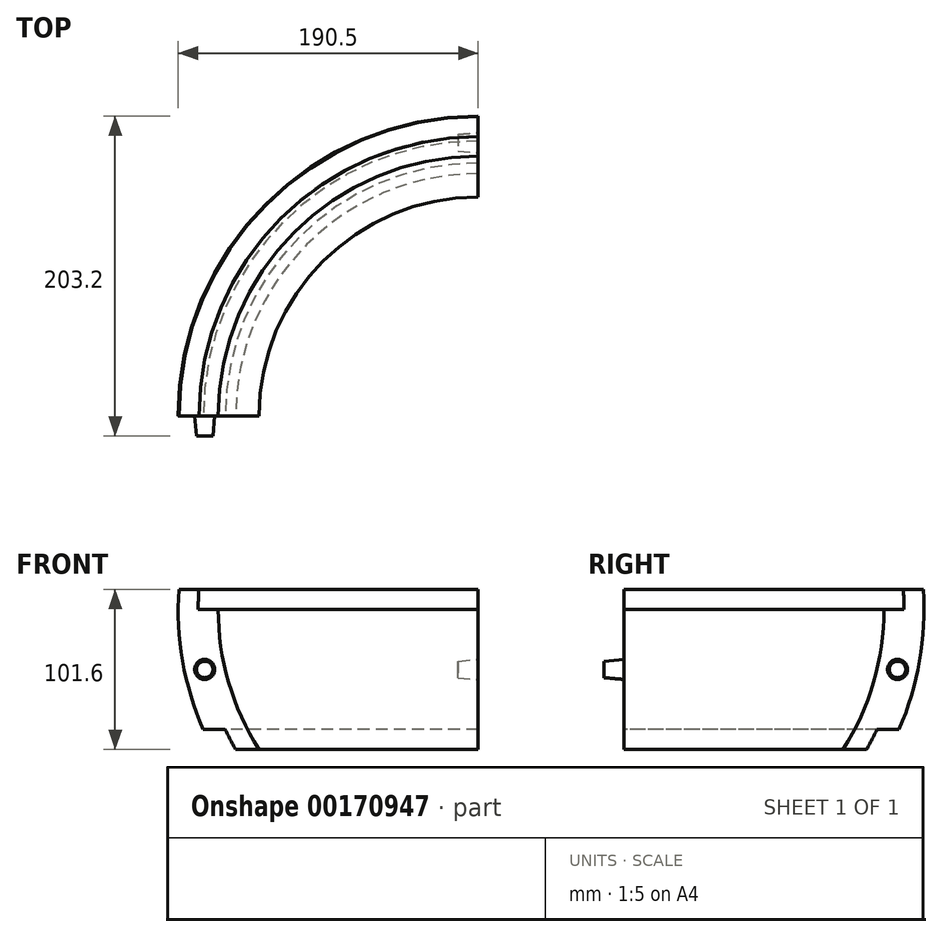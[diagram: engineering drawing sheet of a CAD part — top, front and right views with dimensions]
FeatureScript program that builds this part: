
annotation { "Feature Type Name" : "Feature", "Feature Type Description" : "" }
export const myFeature = defineFeature(function(context is Context, id is Id, definition is map)
    precondition{}
    {
        {
            var Q0;
            Q0=qCreatedBy(makeId("Front.planeOp"),FACE);
            var sketch = newSketch(context, id + "F0", { "sketchPlane" : qUnion([Q0])});
            skLineSegment(sketch, "E0", {"start": v(0, 0) * mm, "end": v(-165.1, 0) * mm});
            skLineSegment(sketch, "E1", {"start": v(0, 0) * mm, "end": v(0, -76.2) * mm});
            skLineSegment(sketch, "E2", {"start": v(0, -76.2) * mm, "end": v(-146.46, -76.2) * mm});
            skLineSegment(sketch, "E3", {"start": v(-190.08, 12.7) * mm, "end": v(-190.08, 12.7) * mm});
            skArc(sketch, "E4", {"start": v(-160.64, -76.2) * mm, "mid": v(-160.63, -76.23) * mm, "end": v(-160.62, -76.26) * mm});
            skArc(sketch, "E5", {"start": v(-190.08, 12.7) * mm, "mid": v(-187.68, -32.68) * mm, "end": v(-174.6, -76.2) * mm});
            skArc(sketch, "E6", {"start": v(-160.62, -76.26) * mm, "mid": v(-157.43, -82.64) * mm, "end": v(-153.98, -88.9) * mm});
            skArc(sketch, "E7", {"start": v(-165.1, 0) * mm, "mid": v(-158.47, -46.3) * mm, "end": v(-139.12, -88.9) * mm});
            skLineSegment(sketch, "E8", {"start": v(-177.35, 12.7) * mm, "end": v(-177.35, 12.7) * mm});
            skArc(sketch, "E9", {"start": v(-177.35, 12.7) * mm, "mid": v(-177.69, 6.35) * mm, "end": v(-177.8, 0) * mm});
            skLineSegment(sketch, "E10", {"start": v(-165.1, 0) * mm, "end": v(-177.7, 0) * mm});
            skLineSegment(sketch, "E11", {"start": v(-177.35, 12.7) * mm, "end": v(-190.08, 12.7) * mm});
            skLineSegment(sketch, "E12", {"start": v(-153.98, -88.9) * mm, "end": v(-139.12, -88.9) * mm});
            skLineSegment(sketch, "E13", {"start": v(-174.6, -76.2) * mm, "end": v(-160.62, -76.26) * mm});
            skLineSegment(sketch, "E14", {"start": v(-177.7, 0) * mm, "end": v(-177.8, 0) * mm});
            skSolve(sketch);
        }
        {
            var Q0;
            Q0=makeQuery(id+"F0.imprint","IMPRINT",FACE,{"disambiguationData":[TD([[makeQuery(id+"F0.imprint","IMPRINT",EDGE,{"derivedFrom":sQuery(id+"F0.wireOp",EDGE,"E5")}),1.0]])]});
            var Q1;
            {var subQ4=sQuery(id+"F0.wireOp",EDGE,"E10");Q1=makeQuery(id+"F0.imprint","IMPRINT",FACE,{"disambiguationData":[TD([[makeQuery(id+"F0.imprint","IMPRINT",EDGE,{"derivedFrom":subQ4}),1.0]])]});}
            var Q2;
            {var subQ4=sQuery(id+"F0.wireOp",EDGE,"E6");Q2=makeQuery(id+"F0.imprint","IMPRINT",FACE,{"disambiguationData":[TD([[makeQuery(id+"F0.imprint","IMPRINT",EDGE,{"derivedFrom":subQ4}),1.0]])]});}
            var Q3;
            Q3=sQuery(id+"F0.wireOp",EDGE,"E1");
            revolve(context, id + "F1", {"entities" : qUnion([Q0, Q1, Q2]), "axis" : qUnion([Q3]), "revolveType" : RevolveType.ONE_DIRECTION, "angle" : 90 * degree});
        }
        {
            var Q0;
            Q0=makeQuery(id+"F0.imprint","IMPRINT",FACE,{"disambiguationData":[TD([[makeQuery(id+"F0.imprint","IMPRINT",EDGE,{"derivedFrom":sQuery(id+"F0.wireOp",EDGE,"E5")}),1.0]])]});
            var sketch = newSketch(context, id + "F2", { "sketchPlane" : qUnion([Q0])});
            skCircle(sketch, "E15", {"center": v(-173.67, -38.1) * mm, "radius": 6.35 * mm});
            skSolve(sketch);
        }
        {
            var Q0;
            Q0 = qSketchRegion(id + "F2", true);
            extrude(context, id + "F3", {"entities" : qUnion([Q0]), "operationType" : NewBodyOperationType.ADD, "depth" : 12.7 * mm, "hasDraft" : true, "draftAngle" : 5 * degree, "draftPullDirection" : true});
        }
        {
            var Q0;
            Q0=makeQuery(id+"F1.opRevolve","CAP_FACE",FACE,{"disambiguationData":[OSD([sQuery(id+"F0.wireOp",EDGE,"E5"),sQuery(id+"F0.wireOp",EDGE,"E6"),sQuery(id+"F0.wireOp",EDGE,"E7"),sQuery(id+"F0.wireOp",EDGE,"E9"),sQuery(id+"F0.wireOp",EDGE,"E10"),sQuery(id+"F0.wireOp",EDGE,"E11"),sQuery(id+"F0.wireOp",EDGE,"E12"),sQuery(id+"F0.wireOp",EDGE,"E13"),sQuery(id+"F0.wireOp",EDGE,"E14")])],"isStart":false});
            var sketch = newSketch(context, id + "F4", { "sketchPlane" : qUnion([Q0])});
            skCircle(sketch, "E16", {"center": v(173.67, -38.1) * mm, "radius": 6.35 * mm});
            skSolve(sketch);
        }
        {
            var Q0;
            Q0 = qSketchRegion(id + "F4", true);
            extrude(context, id + "F5", {"entities" : qUnion([Q0]), "operationType" : NewBodyOperationType.REMOVE, "oppositeDirection" : true, "depth" : 12.7 * mm, "hasDraft" : true, "draftAngle" : 5 * degree, "draftPullDirection" : true});
        }
    });
